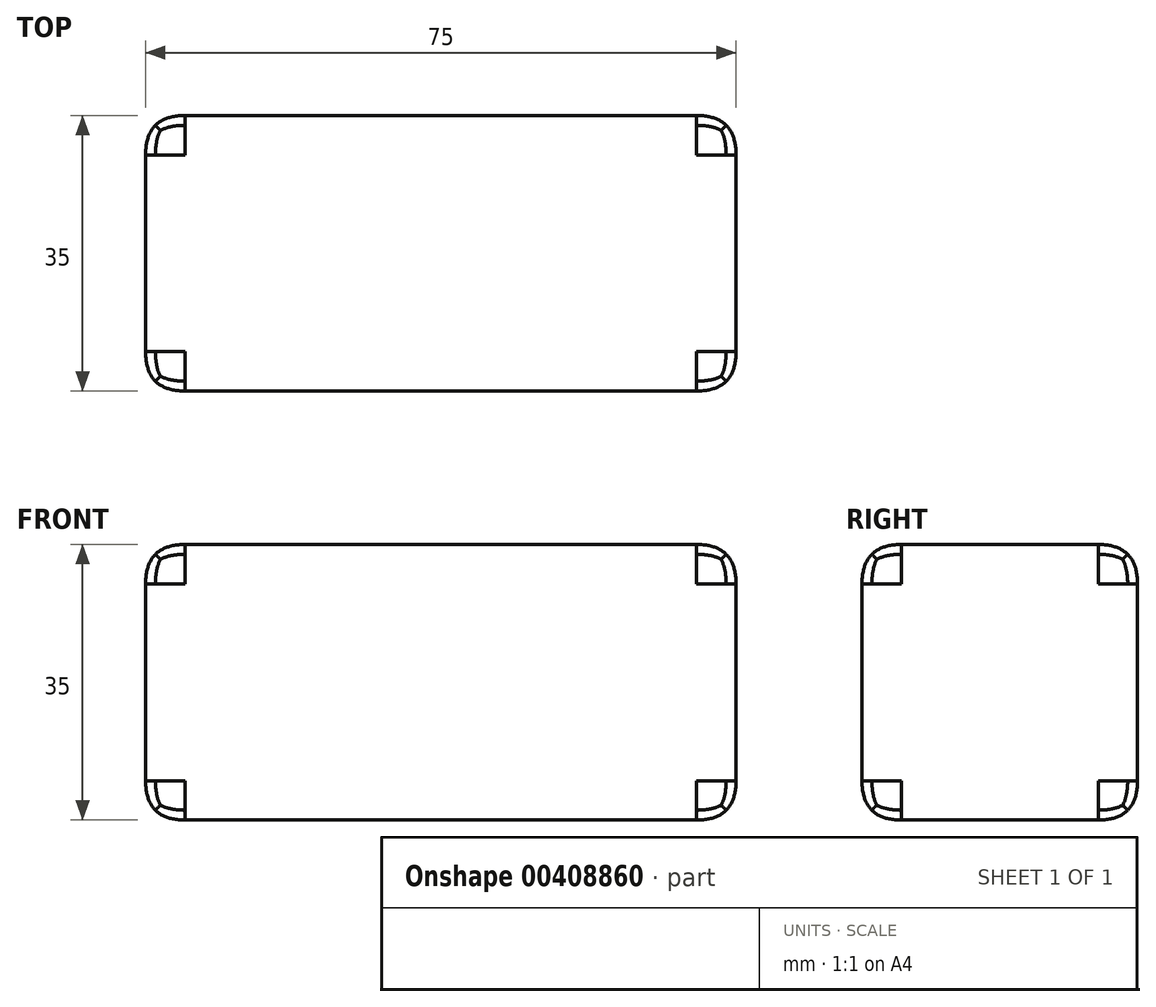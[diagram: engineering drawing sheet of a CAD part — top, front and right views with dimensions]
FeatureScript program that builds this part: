
annotation { "Feature Type Name" : "Feature", "Feature Type Description" : "" }
export const myFeature = defineFeature(function(context is Context, id is Id, definition is map)
    precondition{}
    {
        {
            var Q0;
            Q0=qCreatedBy(makeId("Top.planeOp"),FACE);
            var sketch = newSketch(context, id + "F0", { "sketchPlane" : qUnion([Q0])});
            skLineSegment(sketch, "E0.bottom", {"start": v(37.5, 17.5) * mm, "end": v(-37.5, 17.5) * mm});
            skLineSegment(sketch, "E0.top", {"start": v(37.5, -17.5) * mm, "end": v(-37.5, -17.5) * mm});
            skLineSegment(sketch, "E0.left", {"start": v(37.5, 17.5) * mm, "end": v(37.5, -17.5) * mm});
            skLineSegment(sketch, "E0.right", {"start": v(-37.5, 17.5) * mm, "end": v(-37.5, -17.5) * mm});
            skPoint(sketch, "E0.middle", {"position": v(0, 0) * mm});
            skSolve(sketch);
        }
        {
            var Q0;
            Q0=makeQuery(id+"F0.imprint","IMPRINT",FACE,{"disambiguationData":[TD([[makeQuery(id+"F0.imprint","IMPRINT",EDGE,{"derivedFrom":sQuery(id+"F0.wireOp",EDGE,"E0.bottom")}),1.0]])]});
            extrude(context, id + "F1", {"entities" : qUnion([Q0]), "depth" : 35 * mm});
        }
        {
            var Q0;
            Q0=makeQuery(id+"F1.opExtrude","CAP_FACE",FACE,{"disambiguationData":[OSD([sQuery(id+"F0.wireOp",EDGE,"E0.bottom"),sQuery(id+"F0.wireOp",EDGE,"E0.top"),sQuery(id+"F0.wireOp",EDGE,"E0.left"),sQuery(id+"F0.wireOp",EDGE,"E0.right")])],"isStart":false});
            var Q1;
            Q1=makeQuery(id+"F1.opExtrude","SWEPT_FACE",FACE,{"disambiguationData":[OSD([sQuery(id+"F0.wireOp",EDGE,"E0.top")])]});
            var Q2;
            Q2=makeQuery(id+"F1.opExtrude","SWEPT_FACE",FACE,{"disambiguationData":[OSD([sQuery(id+"F0.wireOp",EDGE,"E0.right")])]});
            var Q3;
            Q3=makeQuery(id+"F1.opExtrude","SWEPT_FACE",FACE,{"disambiguationData":[OSD([sQuery(id+"F0.wireOp",EDGE,"E0.left")])]});
            var Q4;
            Q4=makeQuery(id+"F1.opExtrude","CAP_FACE",FACE,{"disambiguationData":[OSD([sQuery(id+"F0.wireOp",EDGE,"E0.bottom"),sQuery(id+"F0.wireOp",EDGE,"E0.top"),sQuery(id+"F0.wireOp",EDGE,"E0.left"),sQuery(id+"F0.wireOp",EDGE,"E0.right")])],"isStart":true});
            var Q5;
            Q5=makeQuery(id+"F1.opExtrude","SWEPT_FACE",FACE,{"disambiguationData":[OSD([sQuery(id+"F0.wireOp",EDGE,"E0.bottom")])]});
            fillet(context, id + "F2", {"entities" : qUnion([Q0, Q1, Q2, Q3, Q4, Q5]), "radius" : 5 * mm, "rho" : 0.5, "crossSection" : FilletCrossSection.CONIC, "allowEdgeOverflow" : false});
        }
    });
